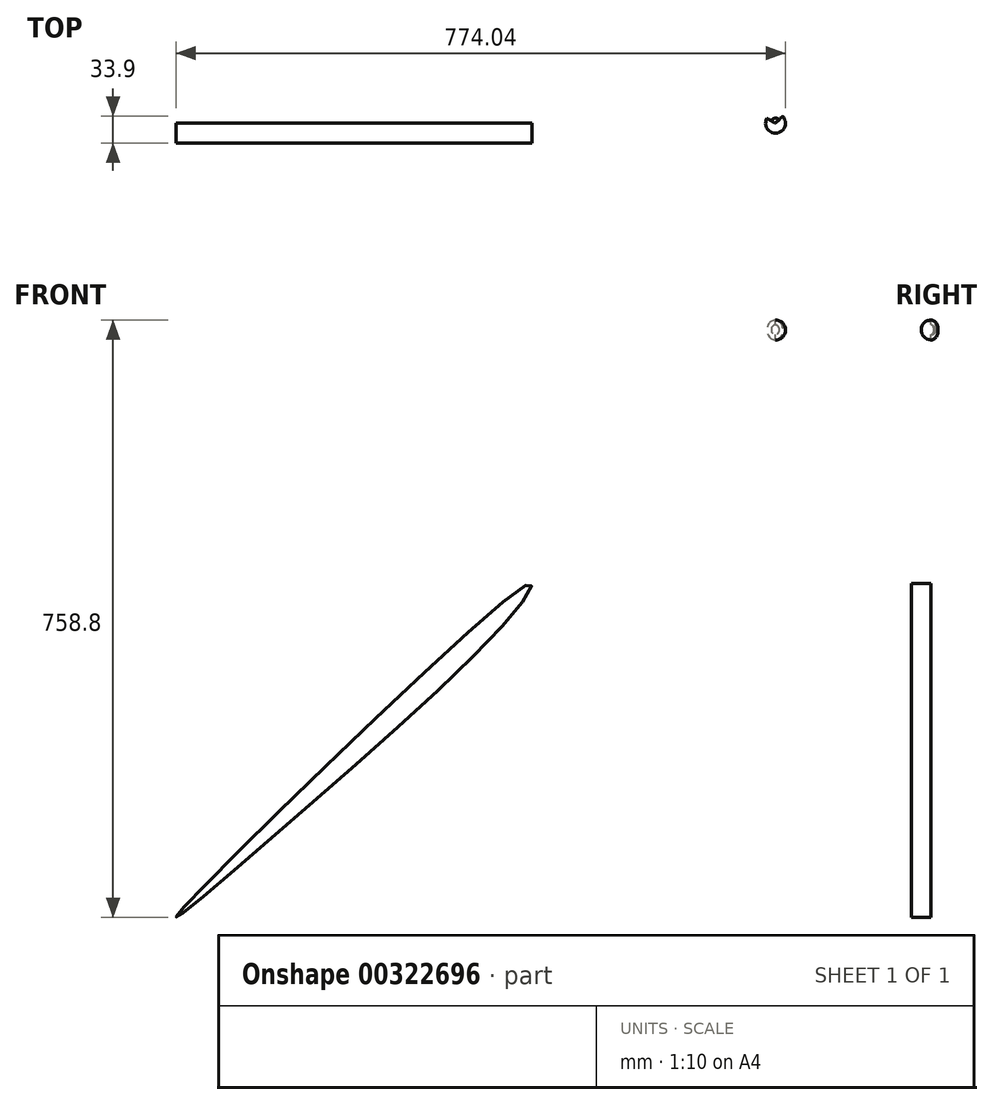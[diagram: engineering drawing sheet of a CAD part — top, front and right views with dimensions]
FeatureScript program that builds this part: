
annotation { "Feature Type Name" : "Feature", "Feature Type Description" : "" }
export const myFeature = defineFeature(function(context is Context, id is Id, definition is map)
    precondition{}
    {
        {
            var Q0;
            Q0=qCreatedBy(makeId("Front.planeOp"),FACE);
            var sketch = newSketch(context, id + "F0", { "sketchPlane" : qUnion([Q0])});
            skLineSegment(sketch, "E0", {"start": v(0, 0) * mm, "end": v(0, 12.7) * mm});
            skArc(sketch, "E1", {"start": v(0, 0) * mm, "mid": v(6.4, 6.35) * mm, "end": v(0, 12.7) * mm});
            skSolve(sketch);
        }
        {
            var Q0;
            Q0=makeQuery(id+"F0.imprint","IMPRINT",FACE,{"disambiguationData":[TD([[makeQuery(id+"F0.imprint","IMPRINT",EDGE,{"derivedFrom":sQuery(id+"F0.wireOp",EDGE,"E0")}),-1.0]])]});
            var Q1;
            Q1=sQuery(id+"F0.wireOp",EDGE,"E0");
            revolve(context, id + "F1", {"entities" : qUnion([Q0]), "axis" : qUnion([Q1]), "revolveType" : RevolveType.FULL});
        }
        {
            var Q0;
            Q0=qCreatedBy(makeId("Front.planeOp"),FACE);
            var sketch = newSketch(context, id + "F2", { "sketchPlane" : qUnion([Q0])});
            skLineSegment(sketch, "E2", {"start": v(0, -6.67) * mm, "end": v(0, 18.73) * mm});
            skArc(sketch, "E3", {"start": v(0, 18.73) * mm, "mid": v(-12.59, 6.03) * mm, "end": v(0, -6.67) * mm});
            skSolve(sketch);
        }
        {
            var Q0;
            Q0=makeQuery(id+"F2.imprint","IMPRINT",FACE,{"disambiguationData":[TD([[makeQuery(id+"F2.imprint","IMPRINT",EDGE,{"derivedFrom":sQuery(id+"F2.wireOp",EDGE,"E2")}),1.0]])]});
            var Q1;
            Q1=sQuery(id+"F2.wireOp",EDGE,"E2");
            revolve(context, id + "F3", {"operationType" : NewBodyOperationType.ADD, "entities" : qUnion([Q0]), "axis" : qUnion([Q1]), "revolveType" : RevolveType.TWO_DIRECTIONS, "angle" : 225 * degree, "angleBack" : 330 * degree});
        }
        {
            var Q0;
            Q0=qCreatedBy(makeId("Front.planeOp"),FACE);
            var sketch = newSketch(context, id + "F4", { "sketchPlane" : qUnion([Q0])});
            skFitSpline(sketch, "E4", {"points": [v(-631.39, -606.41) * mm, v(-761.13, -740.07) * mm, v(-610.79, -614.03) * mm, v(-329.6, -349.84) * mm, v(-311.42, -315.81) * mm, v(-631.39, -606.41) * mm]});
            skSolve(sketch);
        }
        {
            var Q0;
            Q0 = qSketchRegion(id + "F4", true);
            extrude(context, id + "F5", {"entities" : qUnion([Q0]), "depth" : 25 * mm});
        }
    });
